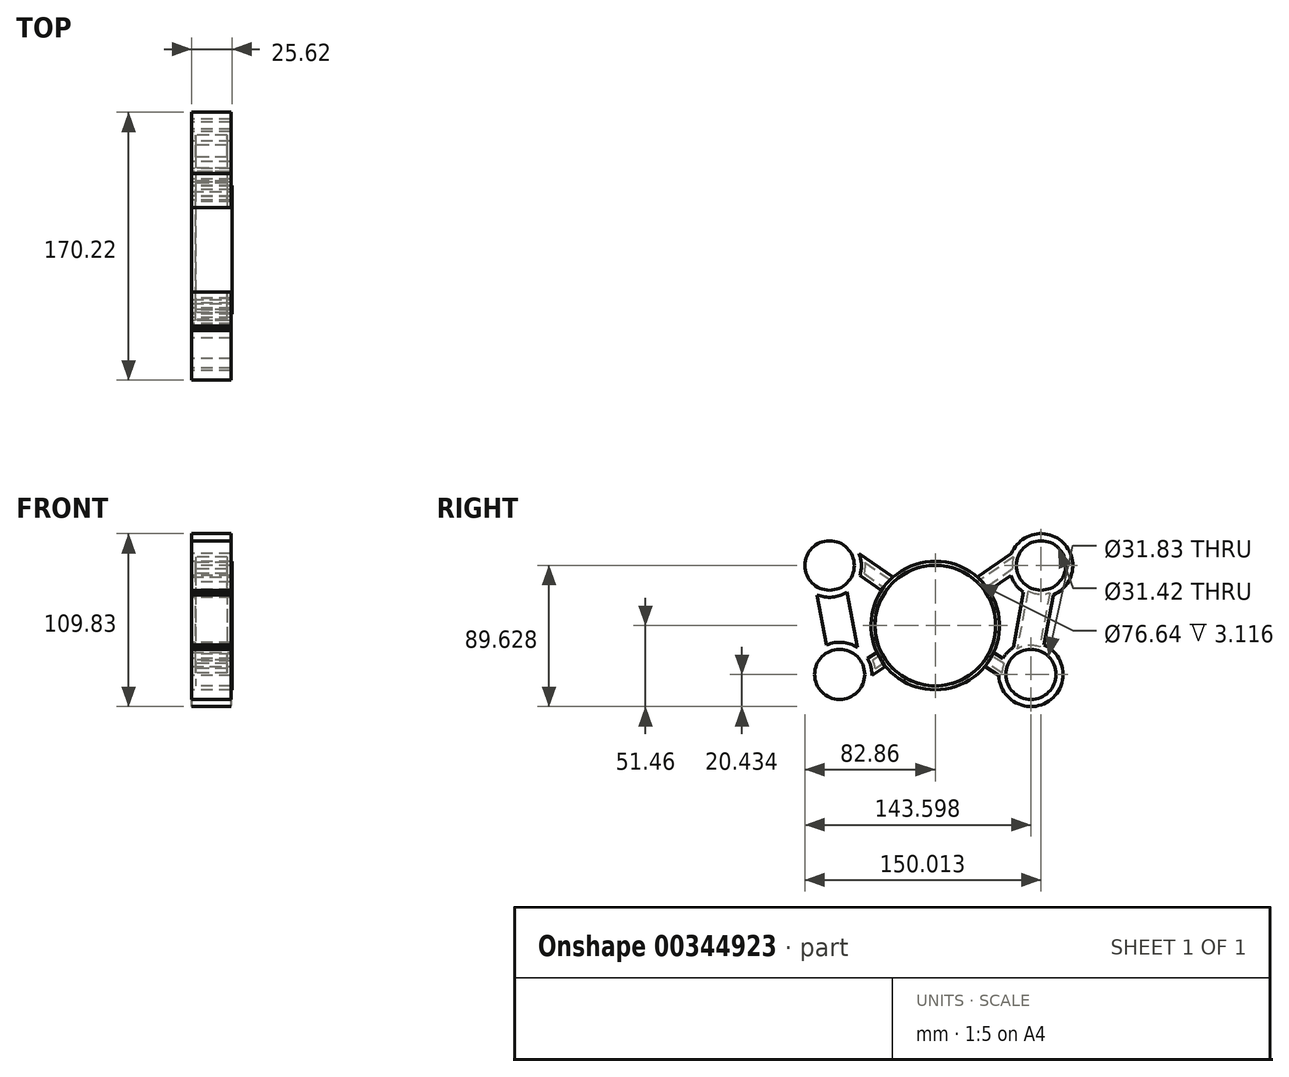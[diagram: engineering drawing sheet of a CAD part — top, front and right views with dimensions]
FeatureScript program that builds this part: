
annotation { "Feature Type Name" : "Feature", "Feature Type Description" : "" }
export const myFeature = defineFeature(function(context is Context, id is Id, definition is map)
    precondition{}
    {
        {
            var Q0;
            Q0=qCreatedBy(makeId("Right.planeOp"),FACE);
            var sketch = newSketch(context, id + "F0", { "sketchPlane" : qUnion([Q0])});
            skCircle(sketch, "E0", {"center": v(0, 0) * mm, "radius": 40.81 * mm});
            skCircle(sketch, "E1", {"center": v(67.15, 38.17) * mm, "radius": 20.2 * mm});
            skCircle(sketch, "E2", {"center": v(67.15, 38.17) * mm, "radius": 15.71 * mm});
            skCircle(sketch, "E3", {"center": v(60.74, -31.03) * mm, "radius": 20.43 * mm});
            skCircle(sketch, "E4", {"center": v(60.74, -31.03) * mm, "radius": 15.92 * mm});
            skLineSegment(sketch, "E5", {"start": v(75.05, 19.57) * mm, "end": v(69.08, -12.37) * mm});
            skLineSegment(sketch, "E6", {"start": v(56.13, 21.23) * mm, "end": v(49.56, -13.92) * mm});
            skLineSegment(sketch, "E7", {"start": v(43.07, -20.76) * mm, "end": v(37.06, -17.1) * mm});
            skLineSegment(sketch, "E8", {"start": v(40.32, -31.7) * mm, "end": v(31.6, -25.82) * mm});
            skLineSegment(sketch, "E9", {"start": v(47.92, 31.97) * mm, "end": v(34.2, 22.27) * mm});
            skLineSegment(sketch, "E10", {"start": v(48.4, 45.67) * mm, "end": v(26.8, 30.78) * mm});
            skLineSegment(sketch, "E11.MirrorCS", {"start": v(-48.4, 45.67) * mm, "end": v(-26.8, 30.78) * mm});
            skLineSegment(sketch, "E12.MirrorCS", {"start": v(-47.92, 31.97) * mm, "end": v(-34.2, 22.27) * mm});
            skLineSegment(sketch, "E13.MirrorCS", {"start": v(-56.13, 21.23) * mm, "end": v(-49.56, -13.92) * mm});
            skLineSegment(sketch, "E14.MirrorCS", {"start": v(-75.05, 19.57) * mm, "end": v(-69.08, -12.37) * mm});
            skCircle(sketch, "E15.MirrorC", {"center": v(-67.15, 38.17) * mm, "radius": 20.2 * mm});
            skCircle(sketch, "E16.MirrorC", {"center": v(-67.15, 38.17) * mm, "radius": 15.71 * mm});
            skCircle(sketch, "E17.MirrorC", {"center": v(-60.74, -31.03) * mm, "radius": 20.43 * mm});
            skCircle(sketch, "E18.MirrorC", {"center": v(-60.74, -31.03) * mm, "radius": 15.92 * mm});
            skLineSegment(sketch, "E19.MirrorCS", {"start": v(-40.32, -31.7) * mm, "end": v(-31.6, -25.82) * mm});
            skLineSegment(sketch, "E20.MirrorCS", {"start": v(-43.07, -20.76) * mm, "end": v(-37.06, -17.1) * mm});
            skSolve(sketch);
        }
        {
            var Q0;
            Q0=makeQuery(id+"F0.imprint","IMPRINT",FACE,{"disambiguationData":[TD([[makeQuery(id+"F0.imprint","IMPRINT",EDGE,{"derivedFrom":sQuery(id+"F0.wireOp",EDGE,"E4")}),-1.0]])]});
            var Q1;
            {var subQ0=sQuery(id+"F0.wireOp",EDGE,"E7");Q1=makeQuery(id+"F0.imprint","IMPRINT",FACE,{"disambiguationData":[TD([[makeQuery(id+"F0.imprint","IMPRINT",EDGE,{"derivedFrom":subQ0}),1.0]])]});}
            var Q2;
            {var subQ0=sQuery(id+"F0.wireOp",EDGE,"E5");Q2=makeQuery(id+"F0.imprint","IMPRINT",FACE,{"disambiguationData":[TD([[makeQuery(id+"F0.imprint","IMPRINT",EDGE,{"derivedFrom":subQ0}),-1.0]])]});}
            var Q3;
            Q3=makeQuery(id+"F0.imprint","IMPRINT",FACE,{"disambiguationData":[TD([[makeQuery(id+"F0.imprint","IMPRINT",EDGE,{"derivedFrom":sQuery(id+"F0.wireOp",EDGE,"E2")}),-1.0]])]});
            var Q4;
            {var subQ0=sQuery(id+"F0.wireOp",EDGE,"E9");Q4=makeQuery(id+"F0.imprint","IMPRINT",FACE,{"disambiguationData":[TD([[makeQuery(id+"F0.imprint","IMPRINT",EDGE,{"derivedFrom":subQ0}),-1.0]])]});}
            var Q5;
            {var subQ0=sQuery(id+"F0.wireOp",EDGE,"E11.MirrorCS");Q5=makeQuery(id+"F0.imprint","IMPRINT",FACE,{"disambiguationData":[TD([[makeQuery(id+"F0.imprint","IMPRINT",EDGE,{"derivedFrom":subQ0}),-1.0]])]});}
            var Q6;
            {var subQ0=sQuery(id+"F0.wireOp",EDGE,"E13.MirrorCS");Q6=makeQuery(id+"F0.imprint","IMPRINT",FACE,{"disambiguationData":[TD([[makeQuery(id+"F0.imprint","IMPRINT",EDGE,{"derivedFrom":subQ0}),-1.0]])]});}
            var Q7;
            Q7=makeQuery(id+"F0.imprint","IMPRINT",FACE,{"disambiguationData":[TD([[makeQuery(id+"F0.imprint","IMPRINT",EDGE,{"derivedFrom":sQuery(id+"F0.wireOp",EDGE,"E16.MirrorC")}),1.0]])]});
            var Q8;
            Q8=makeQuery(id+"F0.imprint","IMPRINT",FACE,{"disambiguationData":[TD([[makeQuery(id+"F0.imprint","IMPRINT",EDGE,{"derivedFrom":sQuery(id+"F0.wireOp",EDGE,"E18.MirrorC")}),1.0]])]});
            var Q9;
            {var subQ0=sQuery(id+"F0.wireOp",EDGE,"E19.MirrorCS");Q9=makeQuery(id+"F0.imprint","IMPRINT",FACE,{"disambiguationData":[TD([[makeQuery(id+"F0.imprint","IMPRINT",EDGE,{"derivedFrom":subQ0}),1.0]])]});}
            var Q10;
            {var subQ0=sQuery(id+"F0.wireOp",EDGE,"E0");var subQ5=makeQuery(id+"F0.imprint","INTERSECT",VERTEX,{"derivedFrom":[subQ0,sQuery(id+"F0.wireOp",EDGE,"E9")]});Q10=makeQuery(id+"F0.imprint","IMPRINT",FACE,{"disambiguationData":[TD([[makeQuery(id+"F0.imprint","IMPRINT",EDGE,{"disambiguationData":[TD([[subQ5,-1.0]])],"derivedFrom":subQ0}),1.0]])]});}
            extrude(context, id + "F1", {"entities" : qUnion([Q0, Q1, Q2, Q3, Q4, Q5, Q6, Q7, Q8, Q9, Q10]), "depth" : 25 * mm});
        }
        {
            var Q0;
            Q0=qCreatedBy(makeId("Right.planeOp"),FACE);
            var sketch = newSketch(context, id + "F2", { "sketchPlane" : qUnion([Q0])});
            skCircle(sketch, "E21", {"center": v(0, 0) * mm, "radius": 40.82 * mm});
            skSolve(sketch);
        }
        {
            var Q0;
            Q0 = qSketchRegion(id + "F2", true);
            extrude(context, id + "F3", {"entities" : qUnion([Q0]), "operationType" : NewBodyOperationType.ADD, "depth" : 50 * mm});
        }
        {
            var Q0;
            Q0=makeQuery(id+"F3.opExtrude","CAP_FACE",FACE,{"disambiguationData":[OSD([sQuery(id+"F2.wireOp",EDGE,"E21")])],"isStart":false});
            fillet(context, id + "F4", {"entities" : qUnion([Q0]), "radius" : 24.38 * mm, "tangentPropagation" : true, "allowEdgeOverflow" : false});
        }
        {
            var Q0;
            Q0=makeQuery(id+"F3.opExtrude","CAP_FACE",FACE,{"disambiguationData":[OSD([sQuery(id+"F2.wireOp",EDGE,"E21")])],"isStart":false});
            var Q1;
            Q1=makeQuery(id+"F4.opFillet","BLEND_FACE",FACE,{"disambiguationData":[OSD([sQuery(id+"F2.wireOp",EDGE,"E21")])]});
            shell(context, id + "F5", {"entities" : qUnion([Q0, Q1]), "thickness" : 2.5 * mm});
        }
    });
